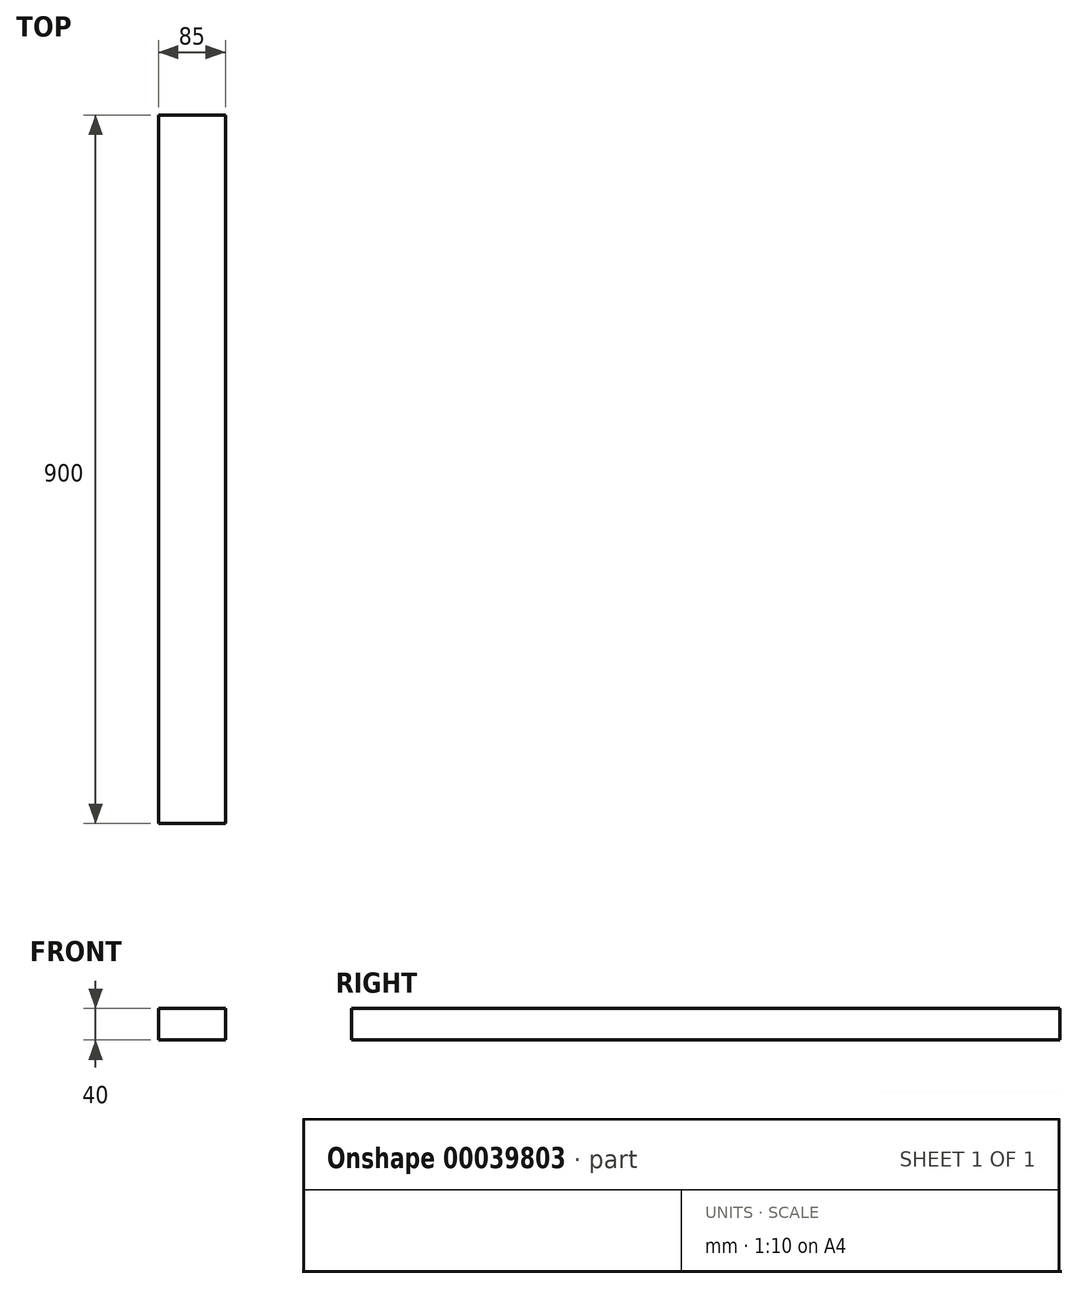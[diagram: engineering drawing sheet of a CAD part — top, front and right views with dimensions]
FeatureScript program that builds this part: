
annotation { "Feature Type Name" : "Feature", "Feature Type Description" : "" }
export const myFeature = defineFeature(function(context is Context, id is Id, definition is map)
    precondition{}
    {
        {
            var Q0;
            Q0=qCreatedBy(makeId("Front.planeOp"),FACE);
            var sketch = newSketch(context, id + "F0", { "sketchPlane" : qUnion([Q0])});
            skLineSegment(sketch, "E0.rect.bottom", {"start": v(42.5, -20) * mm, "end": v(-42.5, -20) * mm});
            skLineSegment(sketch, "E0.rect.top", {"start": v(42.5, 20) * mm, "end": v(-42.5, 20) * mm});
            skLineSegment(sketch, "E0.rect.left", {"start": v(42.5, -20) * mm, "end": v(42.5, 20) * mm});
            skLineSegment(sketch, "E0.rect.right", {"start": v(-42.5, -20) * mm, "end": v(-42.5, 20) * mm});
            skPoint(sketch, "E0.rect.middle", {"position": v(0, 0) * mm});
            skSolve(sketch);
        }
        {
            var Q0;
            Q0 = qSketchRegion(id + "F0", true);
            extrude(context, id + "F1", {"entities" : qUnion([Q0]), "depth" : 900 * mm});
        }
    });
